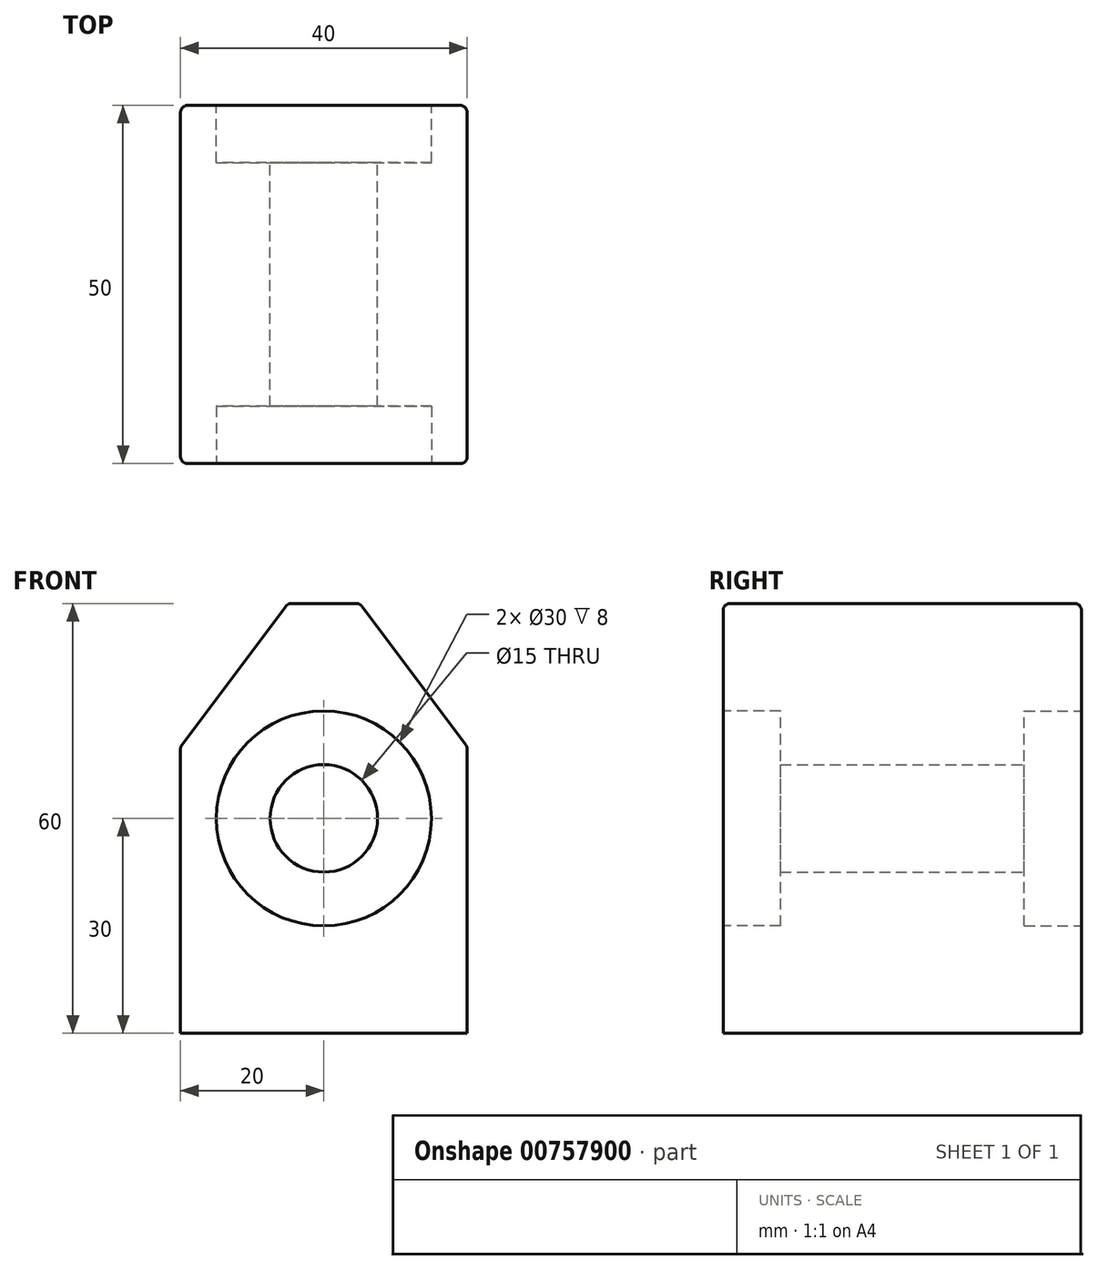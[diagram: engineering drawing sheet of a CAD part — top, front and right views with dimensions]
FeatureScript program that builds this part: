
annotation { "Feature Type Name" : "Feature", "Feature Type Description" : "" }
export const myFeature = defineFeature(function(context is Context, id is Id, definition is map)
    precondition{}
    {
        {
            var Q0;
            Q0=qCreatedBy(makeId("Front.planeOp"),FACE);
            var sketch = newSketch(context, id + "F0", { "sketchPlane" : qUnion([Q0])});
            skLineSegment(sketch, "E0.bottom", {"start": v(20, -30) * mm, "end": v(-20, -30) * mm});
            skLineSegment(sketch, "E0.top", {"start": v(20, 30) * mm, "end": v(-20, 30) * mm});
            skLineSegment(sketch, "E0.left", {"start": v(20, -30) * mm, "end": v(20, 30) * mm});
            skLineSegment(sketch, "E0.right", {"start": v(-20, -30) * mm, "end": v(-20, 30) * mm});
            skPoint(sketch, "E0.middle", {"position": v(0, 0) * mm});
            skCircle(sketch, "E1", {"center": v(0, 0) * mm, "radius": 15 * mm});
            skCircle(sketch, "E2", {"center": v(0, 0) * mm, "radius": 7.5 * mm});
            skSolve(sketch);
        }
        {
            var Q0;
            Q0=makeQuery(id+"F0.imprint","IMPRINT",FACE,{"disambiguationData":[TD([[makeQuery(id+"F0.imprint","IMPRINT",EDGE,{"derivedFrom":sQuery(id+"F0.wireOp",EDGE,"E0.bottom")}),-1.0]])]});
            var Q1;
            Q1=makeQuery(id+"F0.imprint","IMPRINT",FACE,{"disambiguationData":[TD([[makeQuery(id+"F0.imprint","IMPRINT",EDGE,{"derivedFrom":sQuery(id+"F0.wireOp",EDGE,"E1")}),1.0]])]});
            extrude(context, id + "F1", {"entities" : qUnion([Q0, Q1]), "depth" : 50 * mm, "offsetDistance" : 25 * mm});
        }
        {
            var Q0;
            Q0=makeQuery(id+"F0.imprint","IMPRINT",FACE,{"disambiguationData":[TD([[makeQuery(id+"F0.imprint","IMPRINT",EDGE,{"derivedFrom":sQuery(id+"F0.wireOp",EDGE,"E1")}),1.0]])]});
            var Q1;
            Q1=sQuery(id+"F0.wireOp",EDGE,"E1");
            extrude(context, id + "F2", {"entities" : qUnion([Q0]), "operationType" : NewBodyOperationType.REMOVE, "surfaceEntities" : qUnion([Q1]), "depth" : 8 * mm, "offsetDistance" : 25 * mm});
        }
        {
            var Q0;
            Q0=makeQuery(id+"F1.opExtrude","CAP_FACE",FACE,{"disambiguationData":[OSD([sQuery(id+"F0.wireOp",EDGE,"E0.bottom"),sQuery(id+"F0.wireOp",EDGE,"E0.top"),sQuery(id+"F0.wireOp",EDGE,"E0.left"),sQuery(id+"F0.wireOp",EDGE,"E0.right"),sQuery(id+"F0.wireOp",EDGE,"E2")])],"isStart":false});
            var sketch = newSketch(context, id + "F3", { "sketchPlane" : qUnion([Q0])});
            skCircle(sketch, "E3", {"center": v(0, 0) * mm, "radius": 15 * mm});
            skSolve(sketch);
        }
        {
            var Q0;
            Q0 = qSketchRegion(id + "F3", true);
            extrude(context, id + "F4", {"entities" : qUnion([Q0]), "operationType" : NewBodyOperationType.REMOVE, "oppositeDirection" : true, "depth" : 8 * mm, "offsetDistance" : 25 * mm});
        }
        {
            var Q0;
            Q0=makeQuery(id+"F1.opExtrude","SWEPT_EDGE",EDGE,{"disambiguationData":[OSD([sQuery(id+"F0.wireOp",EDGE,"E0.top"),sQuery(id+"F0.wireOp",EDGE,"E0.left")])]});
            var Q1;
            Q1=makeQuery(id+"F1.opExtrude","SWEPT_EDGE",EDGE,{"disambiguationData":[OSD([sQuery(id+"F0.wireOp",EDGE,"E0.top"),sQuery(id+"F0.wireOp",EDGE,"E0.right")])]});
            chamfer(context, id + "F5", {"entities" : qUnion([Q0, Q1]), "chamferType" : ChamferType.TWO_OFFSETS, "width1" : 15 * mm, "oppositeDirection" : false, "width2" : 20 * mm, "tangentPropagation" : true});
        }
        {
            var Q0;
            {var subQ0=sQuery(id+"F0.wireOp",EDGE,"E0.top");Q0=makeQuery(id+"F5.opChamfer","BLEND_EDGE",EDGE,{"blendedFrom":[makeQuery(id+"F1.opExtrude","SWEPT_EDGE",EDGE,{"disambiguationData":[OSD([subQ0,sQuery(id+"F0.wireOp",EDGE,"E0.right")])]}),makeQuery(id+"F1.opExtrude","SWEPT_FACE",FACE,{"disambiguationData":[OSD([subQ0])]})],"blendedInto":[makeQuery(id+"F1.opExtrude","SWEPT_FACE",FACE,{"disambiguationData":[OSD([subQ0])]})]});}
            var Q1;
            {var subQ0=sQuery(id+"F0.wireOp",EDGE,"E0.top");Q1=makeQuery(id+"F5.opChamfer","BLEND_EDGE",EDGE,{"blendedFrom":[makeQuery(id+"F1.opExtrude","SWEPT_EDGE",EDGE,{"disambiguationData":[OSD([subQ0,sQuery(id+"F0.wireOp",EDGE,"E0.left")])]}),makeQuery(id+"F1.opExtrude","SWEPT_FACE",FACE,{"disambiguationData":[OSD([subQ0])]})],"blendedInto":[makeQuery(id+"F1.opExtrude","SWEPT_FACE",FACE,{"disambiguationData":[OSD([subQ0])]})]});}
            var Q2;
            {var subQ0=sQuery(id+"F0.wireOp",EDGE,"E0.left");Q2=makeQuery(id+"F5.opChamfer","BLEND_EDGE",EDGE,{"blendedFrom":[makeQuery(id+"F1.opExtrude","SWEPT_EDGE",EDGE,{"disambiguationData":[OSD([sQuery(id+"F0.wireOp",EDGE,"E0.top"),subQ0])]}),makeQuery(id+"F1.opExtrude","SWEPT_FACE",FACE,{"disambiguationData":[OSD([subQ0])]})],"blendedInto":[makeQuery(id+"F1.opExtrude","SWEPT_FACE",FACE,{"disambiguationData":[OSD([subQ0])]})]});}
            var Q3;
            {var subQ0=sQuery(id+"F0.wireOp",EDGE,"E0.right");var subQ1=sQuery(id+"F0.wireOp",EDGE,"E0.top");Q3=makeQuery(id+"F5.opChamfer","BLEND_EDGE",EDGE,{"blendedFrom":[makeQuery(id+"F1.opExtrude","SWEPT_EDGE",EDGE,{"disambiguationData":[OSD([subQ1,subQ0])]}),makeQuery(id+"F1.opExtrude","CAP_FACE",FACE,{"disambiguationData":[OSD([sQuery(id+"F0.wireOp",EDGE,"E0.bottom"),subQ1,sQuery(id+"F0.wireOp",EDGE,"E0.left"),subQ0,sQuery(id+"F0.wireOp",EDGE,"E2")])],"isStart":true})],"blendedInto":[makeQuery(id+"F1.opExtrude","CAP_FACE",FACE,{"disambiguationData":[OSD([sQuery(id+"F0.wireOp",EDGE,"E0.bottom"),subQ1,sQuery(id+"F0.wireOp",EDGE,"E0.left"),subQ0,sQuery(id+"F0.wireOp",EDGE,"E2")])],"isStart":true})]});}
            var Q4;
            Q4=makeQuery(id+"F1.opExtrude","CAP_EDGE",EDGE,{"disambiguationData":[OSD([sQuery(id+"F0.wireOp",EDGE,"E0.top")])],"isStart":true});
            var Q5;
            {var subQ0=sQuery(id+"F0.wireOp",EDGE,"E0.left");var subQ1=sQuery(id+"F0.wireOp",EDGE,"E0.top");Q5=makeQuery(id+"F5.opChamfer","BLEND_EDGE",EDGE,{"blendedFrom":[makeQuery(id+"F1.opExtrude","SWEPT_EDGE",EDGE,{"disambiguationData":[OSD([subQ1,subQ0])]}),makeQuery(id+"F1.opExtrude","CAP_FACE",FACE,{"disambiguationData":[OSD([sQuery(id+"F0.wireOp",EDGE,"E0.bottom"),subQ1,subQ0,sQuery(id+"F0.wireOp",EDGE,"E0.right"),sQuery(id+"F0.wireOp",EDGE,"E2")])],"isStart":true})],"blendedInto":[makeQuery(id+"F1.opExtrude","CAP_FACE",FACE,{"disambiguationData":[OSD([sQuery(id+"F0.wireOp",EDGE,"E0.bottom"),subQ1,subQ0,sQuery(id+"F0.wireOp",EDGE,"E0.right"),sQuery(id+"F0.wireOp",EDGE,"E2")])],"isStart":true})]});}
            var Q6;
            {var subQ0=sQuery(id+"F0.wireOp",EDGE,"E0.left");var subQ1=sQuery(id+"F0.wireOp",EDGE,"E0.top");Q6=makeQuery(id+"F5.opChamfer","BLEND_EDGE",EDGE,{"blendedFrom":[makeQuery(id+"F1.opExtrude","SWEPT_EDGE",EDGE,{"disambiguationData":[OSD([subQ1,subQ0])]}),makeQuery(id+"F1.opExtrude","CAP_FACE",FACE,{"disambiguationData":[OSD([sQuery(id+"F0.wireOp",EDGE,"E0.bottom"),subQ1,subQ0,sQuery(id+"F0.wireOp",EDGE,"E0.right"),sQuery(id+"F0.wireOp",EDGE,"E2")])],"isStart":false})],"blendedInto":[makeQuery(id+"F1.opExtrude","CAP_FACE",FACE,{"disambiguationData":[OSD([sQuery(id+"F0.wireOp",EDGE,"E0.bottom"),subQ1,subQ0,sQuery(id+"F0.wireOp",EDGE,"E0.right"),sQuery(id+"F0.wireOp",EDGE,"E2")])],"isStart":false})]});}
            var Q7;
            {var subQ0=sQuery(id+"F0.wireOp",EDGE,"E0.right");var subQ1=sQuery(id+"F0.wireOp",EDGE,"E0.top");Q7=makeQuery(id+"F5.opChamfer","BLEND_EDGE",EDGE,{"blendedFrom":[makeQuery(id+"F1.opExtrude","SWEPT_EDGE",EDGE,{"disambiguationData":[OSD([subQ1,subQ0])]}),makeQuery(id+"F1.opExtrude","CAP_FACE",FACE,{"disambiguationData":[OSD([sQuery(id+"F0.wireOp",EDGE,"E0.bottom"),subQ1,sQuery(id+"F0.wireOp",EDGE,"E0.left"),subQ0,sQuery(id+"F0.wireOp",EDGE,"E2")])],"isStart":false})],"blendedInto":[makeQuery(id+"F1.opExtrude","CAP_FACE",FACE,{"disambiguationData":[OSD([sQuery(id+"F0.wireOp",EDGE,"E0.bottom"),subQ1,sQuery(id+"F0.wireOp",EDGE,"E0.left"),subQ0,sQuery(id+"F0.wireOp",EDGE,"E2")])],"isStart":false})]});}
            var Q8;
            Q8=makeQuery(id+"F1.opExtrude","CAP_EDGE",EDGE,{"disambiguationData":[OSD([sQuery(id+"F0.wireOp",EDGE,"E0.top")])],"isStart":false});
            var Q9;
            Q9=makeQuery(id+"F1.opExtrude","CAP_EDGE",EDGE,{"disambiguationData":[OSD([sQuery(id+"F0.wireOp",EDGE,"E0.right")])],"isStart":false});
            var Q10;
            Q10=makeQuery(id+"F1.opExtrude","CAP_EDGE",EDGE,{"disambiguationData":[OSD([sQuery(id+"F0.wireOp",EDGE,"E0.left")])],"isStart":false});
            var Q11;
            Q11=makeQuery(id+"F1.opExtrude","CAP_EDGE",EDGE,{"disambiguationData":[OSD([sQuery(id+"F0.wireOp",EDGE,"E0.left")])],"isStart":true});
            var Q12;
            Q12=makeQuery(id+"F1.opExtrude","CAP_EDGE",EDGE,{"disambiguationData":[OSD([sQuery(id+"F0.wireOp",EDGE,"E0.right")])],"isStart":true});
            var Q13;
            {var subQ0=sQuery(id+"F0.wireOp",EDGE,"E0.right");Q13=makeQuery(id+"F5.opChamfer","BLEND_EDGE",EDGE,{"blendedFrom":[makeQuery(id+"F1.opExtrude","SWEPT_EDGE",EDGE,{"disambiguationData":[OSD([sQuery(id+"F0.wireOp",EDGE,"E0.top"),subQ0])]}),makeQuery(id+"F1.opExtrude","SWEPT_FACE",FACE,{"disambiguationData":[OSD([subQ0])]})],"blendedInto":[makeQuery(id+"F1.opExtrude","SWEPT_FACE",FACE,{"disambiguationData":[OSD([subQ0])]})]});}
            fillet(context, id + "F6", {"entities" : qUnion([Q0, Q1, Q2, Q3, Q4, Q5, Q6, Q7, Q8, Q9, Q10, Q11, Q12, Q13]), "radius" : 1 * mm, "tangentPropagation" : true, "allowEdgeOverflow" : false});
        }
    });
